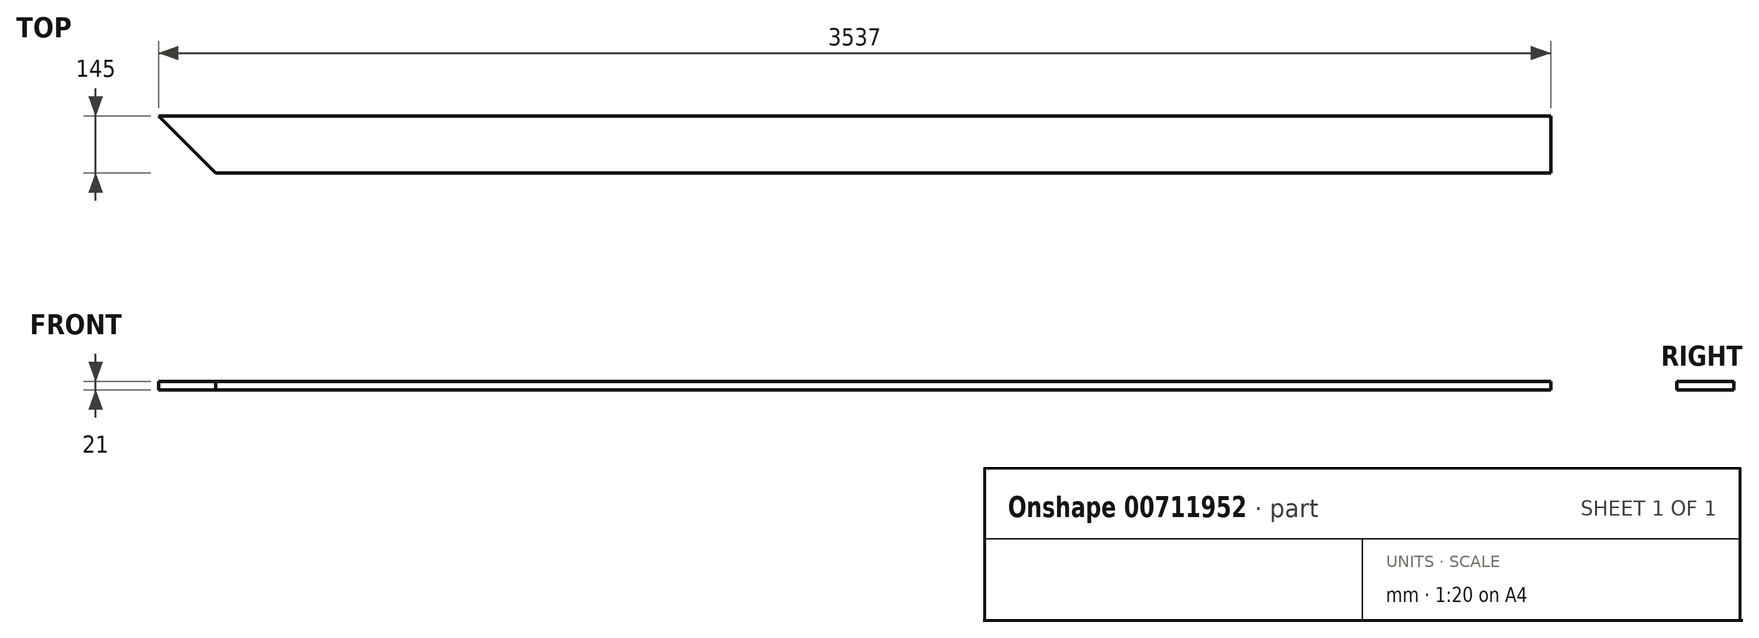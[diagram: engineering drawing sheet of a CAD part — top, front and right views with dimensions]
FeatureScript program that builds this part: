
annotation { "Feature Type Name" : "Feature", "Feature Type Description" : "" }
export const myFeature = defineFeature(function(context is Context, id is Id, definition is map)
    precondition{}
    {
        {
            var Q0;
            Q0=qCreatedBy(makeId("Top.planeOp"),FACE);
            var sketch = newSketch(context, id + "F0", { "sketchPlane" : qUnion([Q0])});
            skLineSegment(sketch, "E0", {"start": v(0, 545.75) * mm, "end": v(0, 690.75) * mm});
            skLineSegment(sketch, "E1", {"start": v(0, 690.75) * mm, "end": v(-3537, 690.75) * mm});
            skLineSegment(sketch, "E2", {"start": v(-3537, 690.75) * mm, "end": v(-3392, 545.75) * mm});
            skLineSegment(sketch, "E3", {"start": v(-3392, 545.75) * mm, "end": v(0, 545.75) * mm});
            skSolve(sketch);
        }
        {
            var Q0;
            Q0 = qSketchRegion(id + "F0", true);
            extrude(context, id + "F1", {"entities" : qUnion([Q0]), "depth" : 21 * mm, "offsetDistance" : 25 * mm});
        }
    });
